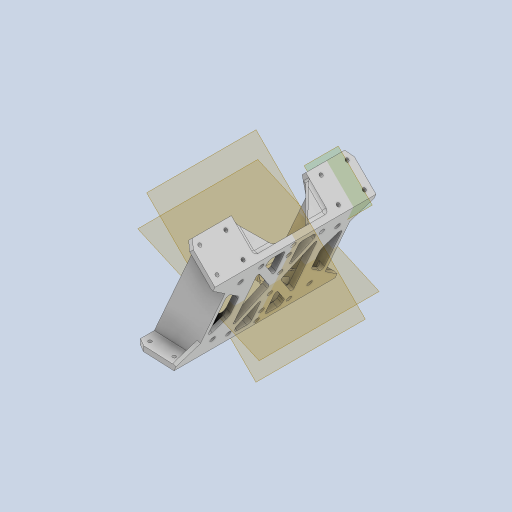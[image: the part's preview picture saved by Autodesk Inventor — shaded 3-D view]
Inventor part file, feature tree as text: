
AUTODESK INVENTOR PART (.ipt)
format: ipt  version: 2023 (Build 270158000, 158)  size: 1,151,488 bytes
history: native  units: mm
features: projected_geometry x31, sketch x20, extrude x18, fillet x10, mirror x8, reference x6, other x6, plane x5, chamfer x4, hole x2
ambient origin geometry x8: Origin, YZ Plane, XZ Plane, XY Plane, X Axis, Y Axis, Z Axis, Center Point
bodies: Solid1 (feature_tree)
feature tree (110):
  sketch  "Sketch1"  dims[d1=3.0mm d2=22.0mm]
  plane  "Work Plane1"
  extrude  "Extrusion1"  Depth=3.0mm
  hole  "Hole1"  [1 undecoded]
  hole  "Hole2"  [1 undecoded]
  sketch  "Sketch4"  dims[d8=2.0mm d9=6.0mm d10=4.0mm d11=2.0mm d12=90.0deg d13=20.0mm d14=0.0mm]
  plane  "Work Plane2"
  extrude  "Extrusion2"  Depth=10.0mm
  plane  "Work Plane3"
  mirror  "Mirror1"
  extrude  "Extrusion3"  Depth=2.0mm TaperAngle=0.0deg
  mirror  "Mirror2"
  extrude  "Extrusion4"  Depth=2.0mm
  extrude  "Extrusion5"  Depth=18.0mm
  plane  "Work Plane4"
  mirror  "Mirror3"
  fillet  "Fillet1"  Radius=18.0mm
  extrude  "Extrusion6"  Depth=2.0mm
  fillet  "Fillet2"  Radius=2.5mm
  fillet  "Fillet3"  Radius=2.5mm
  fillet  "Fillet6"  Radius=2.5mm
  extrude  "Extrusion7"  Depth=2.5mm
  extrude  "Extrusion8"  Depth=500.0mm TaperAngle=0.0deg
  extrude  "Extrusion9"  Depth=2.0mm
  extrude  "Extrusion10"  Depth=2.0mm
  mirror  "Mirror4"
  mirror  "Mirror5"
  extrude  "Extrusion11"  Depth=4.0mm
  extrude  "Extrusion12"  Depth=3.0mm
  extrude  "Extrusion13"  Depth=3.0mm
  extrude  "Extrusion14"  Depth=3.0mm TaperAngle=0.0deg
  extrude  "Extrusion15"  Depth=47.0mm
  mirror  "Mirror6"
  extrude  "Extrusion16"  Depth=3.0mm
  mirror  "Mirror7"
  plane  "Work Plane5"
  extrude  "Extrusion17"  Depth=3.0mm
  mirror  "Mirror8"
  chamfer  "Chamfer2"  Distance=3.0mm
  chamfer  "Chamfer3"  Distance=20.0mm
  chamfer  "Chamfer4"  Distance=4.0mm
  chamfer  "Chamfer5"  Distance=2.5mm
  fillet  "Fillet7"  Radius=2.5mm
  fillet  "Fillet8"  Radius=2.5mm
  fillet  "Fillet9"  Radius=2.5mm
  fillet  "Fillet10"  Radius=4.0mm
  fillet  "Fillet11"  Radius=2.0mm
  fillet  "Fillet12"  Radius=1.0mm
  extrude  "Extrusion18"  Depth=3.0mm TaperAngle=0.0deg
  reference  "Reference1"
  reference  "Reference2"
  sketch  "Sketch2"  dims[d4=3.0mm d5=22.0mm]
  reference  "Reference3"
  reference  "Reference4"
  sketch  "Sketch3"  dims[d6=10.0mm d7=0.0mm]
  reference  "Reference5"
  reference  "Reference6"
  projected_geometry  "Projected Loop1"
  projected_geometry  "Projected Loop2"
  sketch  "Sketch5"  dims[d15=2.0mm d16=6.0mm d17=4.0mm d18=2.0mm d19=90.0deg d20=20.0mm d21=0.0mm d22=3.0mm]
  projected_geometry  "Projected Loop3"
  projected_geometry  "Projected Loop4"
  sketch  "Sketch6"  dims[d23=10.0mm d24=0.0mm d25=10.0mm]
  projected_geometry  "Projected Loop5"
  projected_geometry  "Projected Loop6"
  projected_geometry  "Projected Loop7"
  projected_geometry  "Projected Loop8"
  projected_geometry  "Projected Loop9"
  sketch  "Sketch7"  dims[d26=10.0mm d27=2.0mm d28=0.0mm]
  projected_geometry  "Projected Loop10"
  projected_geometry  "Projected Loop11"
  projected_geometry  "Projected Loop12"
  projected_geometry  "Projected Loop13"
  projected_geometry  "Projected Loop14"
  sketch  "Sketch8"  dims[d29=2.0mm d30=0.0mm d31=15.0mm]
  projected_geometry  "Projected Loop15"
  sketch  "Sketch9"  dims[d32=15.0mm d33=18.0mm d34=18.0mm]
  projected_geometry  "Projected Loop16"
  sketch  "Sketch10"  dims[d35=2.0mm d36=0.0mm d40=2.0mm d41=2.5mm d42=2.5mm d43=2.5mm]
  projected_geometry  "Projected Loop17"
  sketch  "Sketch11"  dims[d44=2.5mm d45=2.5mm]
  projected_geometry  "Projected Loop18"
  sketch  "Sketch12"  dims[d46=2.5mm d47=500.0mm d48=0.0mm]
  projected_geometry  "Projected Loop19"
  sketch  "Sketch13"  dims[d49=0.7mm d50=2.0mm]
  projected_geometry  "Projected Loop20"
  sketch  "Sketch14"  dims[d53=2.0mm d54=4.0mm]
  projected_geometry  "Projected Loop21"
  projected_geometry  "Projected Loop22"
  sketch  "Sketch15"  dims[d55=7.0mm d56=4.0mm]
  projected_geometry  "Projected Loop23"
  projected_geometry  "Projected Loop24"
  sketch  "Sketch16"  dims[d57=7.0mm d58=3.0mm]
  projected_geometry  "Projected Loop25"
  sketch  "Sketch17"  dims[d59=3.0mm d60=3.0mm]
  projected_geometry  "Projected Loop26"
  sketch  "Sketch18"  dims[d61=3.0mm d62=500.0mm d63=0.0mm]
  projected_geometry  "Projected Loop27"
  projected_geometry  "Projected Loop28"
  sketch  "Sketch20"  dims[d64=35.0mm d65=47.0mm]
  projected_geometry  "Projected Loop29"
  projected_geometry  "Projected Loop30"
  sketch  "Sketch21"  dims[d66=3.0mm d67=3.0mm d68=3.0mm d69=3.0mm d70=20.0mm d71=0.0mm d72=4.0mm d73=2.5mm d74=2.5mm d75=2.5mm d76=2.5mm d78=4.0mm d79=2.0mm d80=1.0mm d81=20.0mm d82=0.0mm d83=30.0deg d84=5.0mm d85=4.0mm d86=4.0mm d87=1.0mm d88=2.0mm d89=20.0mm d90=0.0mm d91=12.0mm d92=12.0mm d93=3.0mm d94=3.0mm d95=20.0mm d96=0.0mm d97=15.0mm d98=0.0mm d99=15.0mm d100=0.0mm d101=15.0mm d102=15.0mm d103=2.0mm d104=2.0mm d105=20.0mm d106=0.0mm d107=15.0mm d108=15.0mm d109=2.0mm d110=2.0mm d111=20.0mm d112=0.0mm d113=20.0mm d114=20.0mm d115=20.0mm d116=0.0mm d117=-13.0mm d118=2.5mm d119=0.0mm d128=2.5mm d129=2.0mm d130=60.0deg d131=2.5mm d132=2.0mm d133=60.0deg d134=2.5mm d135=2.0mm d136=60.0deg d137=2.5mm d138=2.0mm d139=60.0deg d140=4.0mm d141=1.5mm d142=1.5mm d143=20.0mm d144=2.0mm d145=1.5mm d146=56.0mm d147=40.0mm d148=3.0mm d149=3.0mm d150=3.0mm d151=3.0mm d152=4.0mm d153=0.0mm]
  projected_geometry  "Projected Loop31"
  parser-record x1  (decoder bookkeeping rows leaked as tree rows — omitted from the tree; the rows remain in map.json)
  other  "body_8d_1.iam"
  other  "leg_1_2d_MIR:2"
  other  "leg_holder_2_MIR:1"
  other  "leg_2d_1:1"
  other  "leg_holder_2:1"
note: 2 required parameter values undecoded (feature->parameter linkage not recoverable at this tier; creation-order binding heuristic only, values carry confidence <= 0.55)
note: 1 file-system path scrubbed to <path> (originals preserved in map.json)
